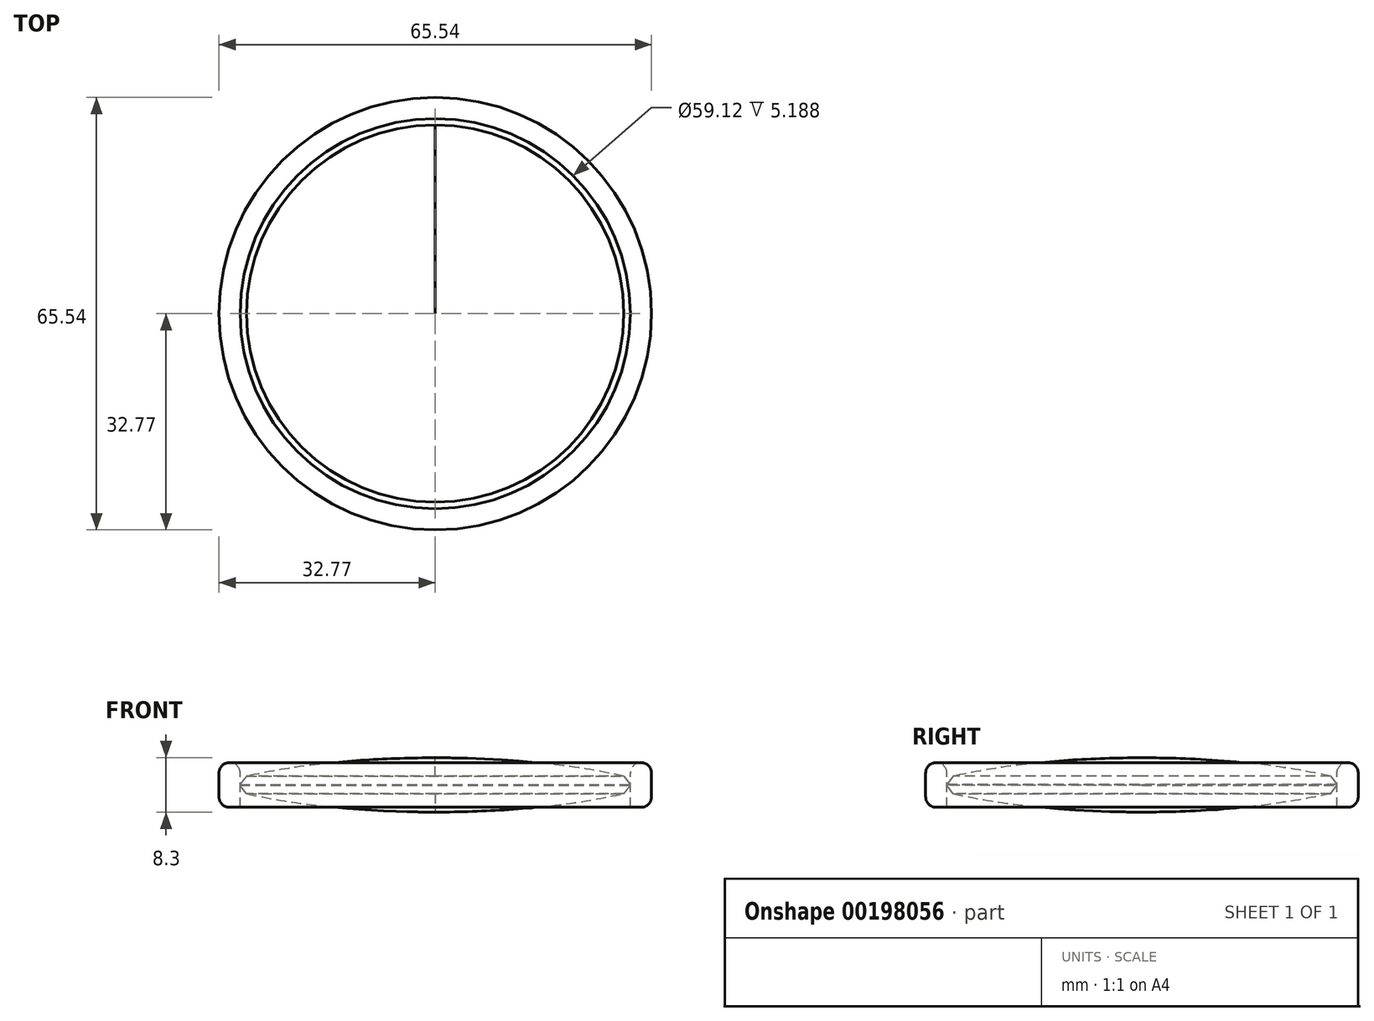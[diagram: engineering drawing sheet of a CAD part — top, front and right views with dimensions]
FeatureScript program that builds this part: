
annotation { "Feature Type Name" : "Feature", "Feature Type Description" : "" }
export const myFeature = defineFeature(function(context is Context, id is Id, definition is map)
    precondition{}
    {
        {
            var Q0;
            Q0=qCreatedBy(makeId("Right.planeOp"),FACE);
            var sketch = newSketch(context, id + "F0", { "sketchPlane" : qUnion([Q0])});
            skLineSegment(sketch, "E0.bottom", {"start": v(29.56, 3.4) * mm, "end": v(32.77, 3.4) * mm});
            skLineSegment(sketch, "E0.top", {"start": v(29.56, -3.4) * mm, "end": v(32.77, -3.4) * mm});
            skLineSegment(sketch, "E0.left", {"start": v(29.56, 3.4) * mm, "end": v(29.56, -3.4) * mm});
            skLineSegment(sketch, "E0.right", {"start": v(32.77, 3.4) * mm, "end": v(32.77, -3.4) * mm});
            skPoint(sketch, "E1.orphan", {"position": v(29.56, 0) * mm});
            skFitSpline(sketch, "E2", {"points": [v(29.56, 1.1) * mm, v(0, 4.15) * mm, v(-0.68, 4.73) * mm], "startDerivative": vector(-47.95, 11.2) * mm, "endDerivative": vector(-0.09, 10.74) * mm});
            skLineSegment(sketch, "E3", {"start": v(0, 0) * mm, "end": v(29.56, 0) * mm, "construction": true});
            skFitSpline(sketch, "E4.MirrorCS", {"points": [v(29.56, -1.1) * mm, v(0, -4.15) * mm, v(-0.68, -4.73) * mm], "startDerivative": vector(-47.95, -11.2) * mm, "endDerivative": vector(-0.09, -10.74) * mm});
            skLineSegment(sketch, "E5.MirrorCS", {"start": v(29.56, -3.4) * mm, "end": v(29.56, 3.4) * mm});
            skLineSegment(sketch, "E6", {"start": v(0, 4.15) * mm, "end": v(0, 0) * mm});
            skLineSegment(sketch, "E7.MirrorCS", {"start": v(0, -4.15) * mm, "end": v(0, 0) * mm});
            skSolve(sketch);
        }
        {
            var Q0;
            {var subQ3=sQuery(id+"F0.wireOp",EDGE,"E0.bottom");Q0=makeQuery(id+"F0.imprint","IMPRINT",FACE,{"disambiguationData":[TD([[makeQuery(id+"F0.imprint","IMPRINT",EDGE,{"derivedFrom":subQ3}),-1.0]])]});}
            var Q1;
            Q1=sQuery(id+"F0.wireOp",EDGE,"E6");
            revolve(context, id + "F1", {"entities" : qUnion([Q0]), "axis" : qUnion([Q1]), "revolveType" : RevolveType.FULL});
        }
        {
            var Q0;
            {var subQ1=sQuery(id+"F0.wireOp",EDGE,"E2");Q0=makeQuery(id+"F0.imprint","IMPRINT",FACE,{"disambiguationData":[TD([[makeQuery(id+"F0.imprint","IMPRINT",EDGE,{"derivedFrom":subQ1}),1.0]])]});}
            var Q1;
            Q1=sQuery(id+"F0.wireOp",EDGE,"E6");
            revolve(context, id + "F2", {"entities" : qUnion([Q0]), "axis" : qUnion([Q1]), "revolveType" : RevolveType.FULL});
        }
        {
            var Q0;
            Q0=makeQuery(id+"F1.opRevolve","SWEPT_EDGE",EDGE,{"disambiguationData":[OSD([sQuery(id+"F0.wireOp",EDGE,"E0.bottom"),sQuery(id+"F0.wireOp",EDGE,"E5.MirrorCS")])]});
            var Q1;
            Q1=makeQuery(id+"F1.opRevolve","SWEPT_EDGE",EDGE,{"disambiguationData":[OSD([sQuery(id+"F0.wireOp",EDGE,"E0.bottom"),sQuery(id+"F0.wireOp",EDGE,"E0.right")])]});
            var Q2;
            Q2=makeQuery(id+"F1.opRevolve","SWEPT_EDGE",EDGE,{"disambiguationData":[OSD([sQuery(id+"F0.wireOp",EDGE,"E0.top"),sQuery(id+"F0.wireOp",EDGE,"E0.right")])]});
            fillet(context, id + "F3", {"entities" : qUnion([Q0, Q1, Q2]), "radius" : 1.6 * mm, "tangentPropagation" : true, "allowEdgeOverflow" : false});
        }
        {
            var Q0;
            Q0=makeQuery(id+"F2.opRevolve","SWEPT_EDGE",EDGE,{"disambiguationData":[OSD([sQuery(id+"F0.wireOp",EDGE,"E2"),sQuery(id+"F0.wireOp",EDGE,"E5.MirrorCS")])]});
            var Q1;
            Q1=makeQuery(id+"F2.opRevolve","SWEPT_EDGE",EDGE,{"disambiguationData":[OSD([sQuery(id+"F0.wireOp",EDGE,"E4.MirrorCS"),sQuery(id+"F0.wireOp",EDGE,"E5.MirrorCS")])]});
            chamfer(context, id + "F4", {"entities" : qUnion([Q0, Q1]), "width" : 1 * mm, "tangentPropagation" : true});
        }
    });
